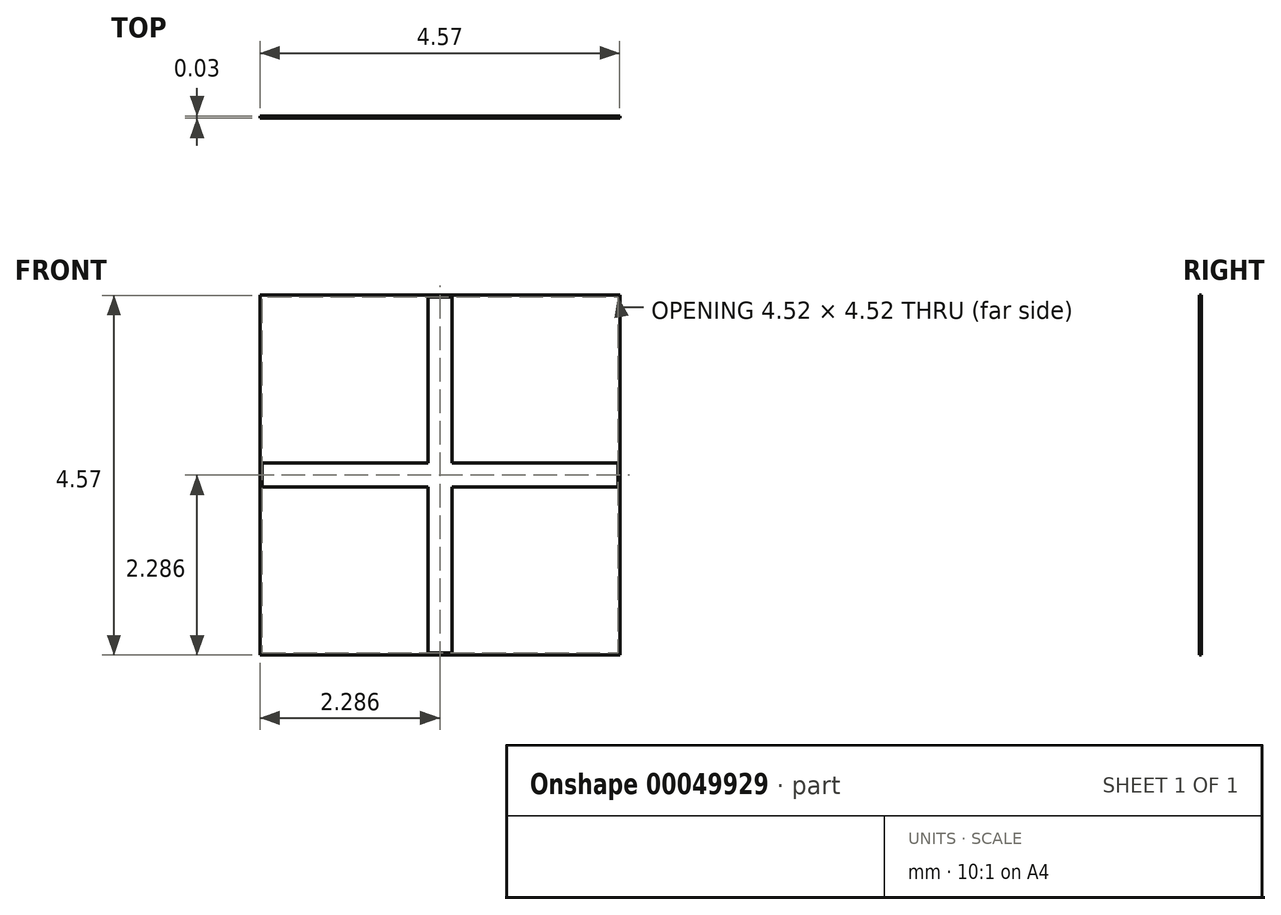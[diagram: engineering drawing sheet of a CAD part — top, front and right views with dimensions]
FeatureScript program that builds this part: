
annotation { "Feature Type Name" : "Feature", "Feature Type Description" : "" }
export const myFeature = defineFeature(function(context is Context, id is Id, definition is map)
    precondition{}
    {
        {
            var Q0;
            Q0=qCreatedBy(makeId("Front.planeOp"),FACE);
            var sketch = newSketch(context, id + "F0", { "sketchPlane" : qUnion([Q0])});
            skLineSegment(sketch, "E0", {"start": v(0, 0) * mm, "end": v(4.57, 0) * mm});
            skLineSegment(sketch, "E1", {"start": v(4.57, 0) * mm, "end": v(4.57, 4.57) * mm});
            skLineSegment(sketch, "E2", {"start": v(4.57, 4.57) * mm, "end": v(0, 4.57) * mm});
            skLineSegment(sketch, "E3", {"start": v(0, 4.57) * mm, "end": v(0, 0) * mm});
            skLineSegment(sketch, "E4", {"start": v(2.29, 4.57) * mm, "end": v(2.29, 0) * mm});
            skLineSegment(sketch, "E5", {"start": v(4.57, 2.29) * mm, "end": v(0, 2.29) * mm});
            skLineSegment(sketch, "E6", {"start": v(0, 2.29) * mm, "end": v(0, 2.13) * mm});
            skLineSegment(sketch, "E7", {"start": v(0, 2.29) * mm, "end": v(0, 2.44) * mm});
            skLineSegment(sketch, "E8", {"start": v(0, 2.44) * mm, "end": v(4.57, 2.44) * mm});
            skLineSegment(sketch, "E9", {"start": v(0, 2.13) * mm, "end": v(4.57, 2.13) * mm});
            skLineSegment(sketch, "E10", {"start": v(0, 2.44) * mm, "end": v(0.03, 2.44) * mm});
            skLineSegment(sketch, "E11", {"start": v(0.03, 2.44) * mm, "end": v(0.03, 2.13) * mm});
            skLineSegment(sketch, "E12", {"start": v(4.57, 2.44) * mm, "end": v(4.55, 2.44) * mm});
            skLineSegment(sketch, "E13", {"start": v(4.55, 2.44) * mm, "end": v(4.55, 2.13) * mm});
            skLineSegment(sketch, "E14", {"start": v(2.29, 4.57) * mm, "end": v(2.28, 4.57) * mm});
            skLineSegment(sketch, "E15", {"start": v(2.29, 4.57) * mm, "end": v(2.32, 4.57) * mm});
            skLineSegment(sketch, "E16", {"start": v(2.29, 4.57) * mm, "end": v(2.44, 4.57) * mm});
            skLineSegment(sketch, "E17", {"start": v(2.29, 4.57) * mm, "end": v(2.27, 4.57) * mm});
            skLineSegment(sketch, "E18", {"start": v(2.29, 4.57) * mm, "end": v(2.13, 4.57) * mm});
            skLineSegment(sketch, "E19", {"start": v(2.13, 4.57) * mm, "end": v(2.13, 0) * mm});
            skLineSegment(sketch, "E20", {"start": v(2.44, 4.57) * mm, "end": v(2.44, 0) * mm});
            skLineSegment(sketch, "E21", {"start": v(2.44, 0) * mm, "end": v(2.44, 0.03) * mm});
            skLineSegment(sketch, "E22", {"start": v(2.44, 0.03) * mm, "end": v(2.13, 0.03) * mm});
            skLineSegment(sketch, "E23", {"start": v(2.44, 4.57) * mm, "end": v(2.44, 4.53) * mm});
            skLineSegment(sketch, "E24", {"start": v(2.13, 4.57) * mm, "end": v(2.13, 4.55) * mm});
            skLineSegment(sketch, "E25", {"start": v(2.13, 4.55) * mm, "end": v(2.44, 4.55) * mm});
            skSolve(sketch);
        }
        {
            var Q0;
            Q0 = qSketchRegion(id + "F0", true);
            extrude(context, id + "F1", {"entities" : qUnion([Q0]), "depth" : 0.03 * mm});
        }
    });
